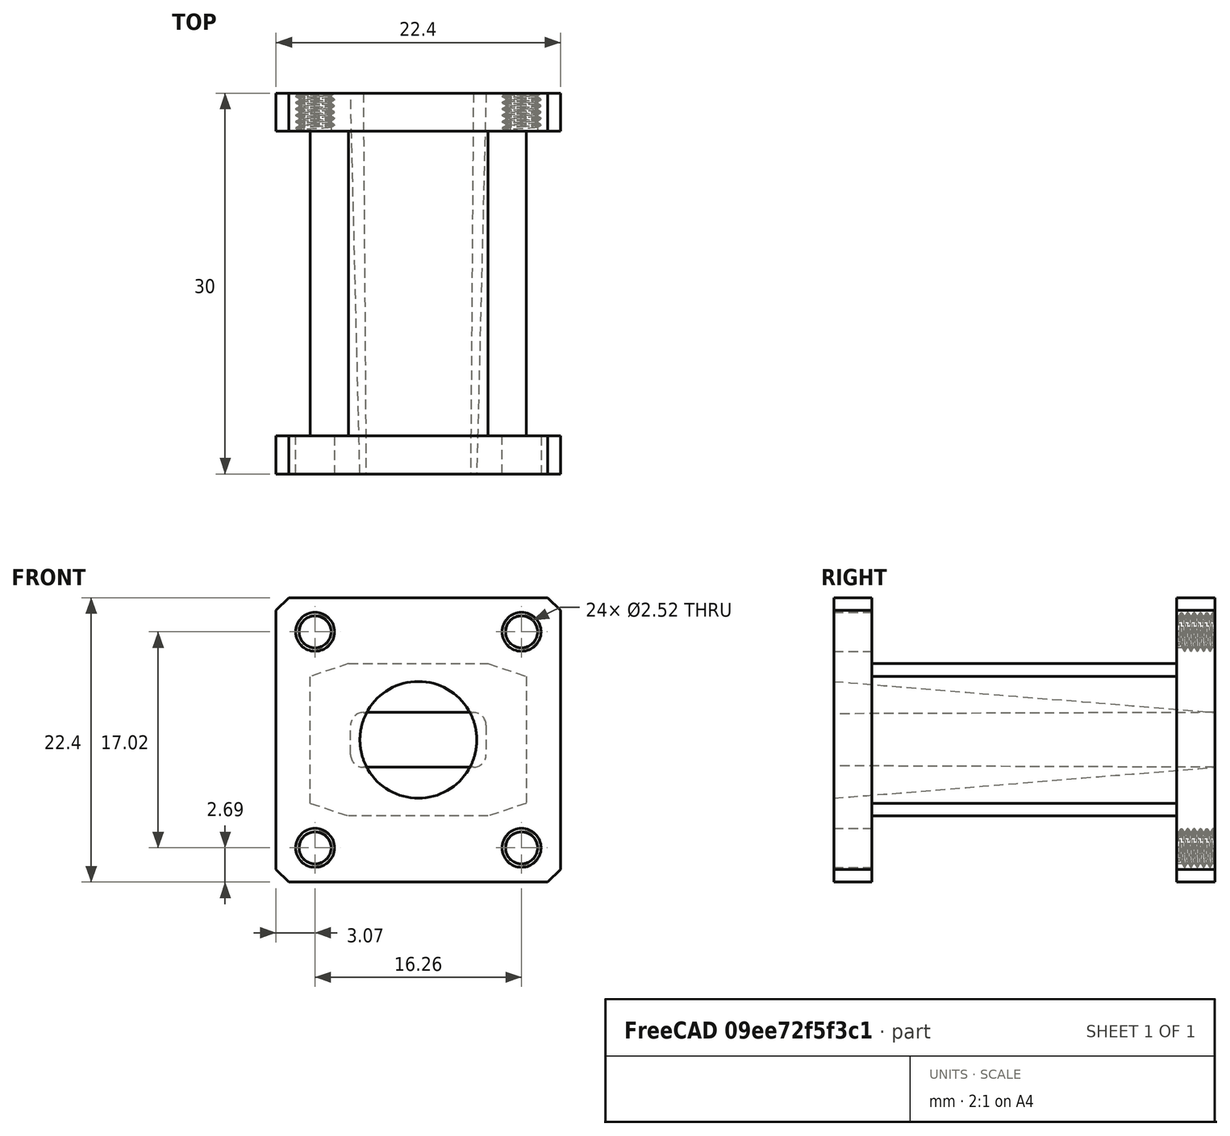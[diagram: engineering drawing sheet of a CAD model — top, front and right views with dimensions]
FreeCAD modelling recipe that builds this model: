
FCSTD DOCUMENT  (FreeCAD 0.21R33771 (Git))
Label: WR42-W1GHZ-circular
License: All rights reserved
LicenseURL: https://en.wikipedia.org/wiki/All_rights_reserved
objects: PartDesign::Chamfer×12, Sketcher::SketchObject×6, PartDesign::Pad×3, TechDraw::DrawViewBalloon×2, PartDesign::Hole×1, TechDraw::DrawSVGTemplate×1, PartDesign::SubtractiveLoft×1, PartDesign::Body×1, TechDraw::DrawViewPart×1, TechDraw::DrawPage×1
note: 41 computed .brp shape members not serialized (recipe doc carries the construction recipe); baked Part::Feature solids carry a one-line shape summary decoded from their .brp

FEATURE [Sketcher::SketchObject] Sketch
  FullyConstrained = true
  MapMode = 5
  Placement = pos=(0,0,0) rot=(1,0,0;1.5708rad)
  Support = -> [XZ_Plane]
  sketch-geometry (9):
    g0: LineSegment StartX=-11.2 StartY=11.2 StartZ=0 EndX=-11.2 EndY=-11.2 EndZ=0
    g1: LineSegment StartX=-11.2 StartY=-11.2 StartZ=0 EndX=11.2 EndY=-11.2 EndZ=0
    g2: LineSegment StartX=11.2 StartY=-11.2 StartZ=0 EndX=11.2 EndY=11.2 EndZ=0
    g3: LineSegment StartX=11.2 StartY=11.2 StartZ=0 EndX=-11.2 EndY=11.2 EndZ=0
    g4: GeomPoint X=0 Y=0 Z=0
    g5: Circle CenterX=-8.13 CenterY=8.51 CenterZ=0 NormalX=0 NormalY=0 NormalZ=1 AngleXU=0 Radius=1.535
    g6: Circle CenterX=8.13 CenterY=8.51 CenterZ=0 NormalX=0 NormalY=0 NormalZ=1 AngleXU=0 Radius=1.535
    g7: Circle CenterX=8.13 CenterY=-8.51 CenterZ=0 NormalX=0 NormalY=0 NormalZ=1 AngleXU=0 Radius=1.535
    g8: Circle CenterX=-8.13 CenterY=-8.51 CenterZ=0 NormalX=0 NormalY=0 NormalZ=1 AngleXU=0 Radius=1.535
  constraints (24):
    c: Coincident(g0,g1)
    c: Coincident(g1,g2)
    c: Coincident(g2,g3)
    c: Coincident(g3,g0)
    c: Horizontal(g1)
    c: Horizontal(g3)
    c: Vertical(g0)
    c: Vertical(g2)
    c: Symmetric(g1,g0,g4)
    c: Coincident(g4,g-1)
    c: DistanceY(g2,g2) = 22.4
    c: DistanceX(g3,g3) = 22.4
    c: Diameter(g5) = 3.07
    c: Equal(g5,g6)
    c: Equal(g5,g8)
    c: Equal(g5,g7)
    c: DistanceX(g4,g6) = 8.13
    c: DistanceX(g5,g4) = 8.13
    c: DistanceX(g8,g4) = 8.13
    c: DistanceX(g4,g7) = 8.13
    c: DistanceY(g4,g5) = 8.51
    c: DistanceY(g4,g6) = 8.51
    c: DistanceY(g7,g4) = 8.51
    c: DistanceY(g8,g4) = 8.51
FEATURE [PartDesign::Pad] Pad
  Direction = (0,-1,-2e-16)
  Length = 3
  Length2 = 10
  Placement = pos=(0,0,0) rot=(1,0,0;1.5708rad)
  Profile = -> Sketch
  ReferenceAxis = -> Sketch [N_Axis]
  Type = 0
FEATURE [PartDesign::Chamfer] Chamfer
  Angle = 45
  Base = -> Pad [Edge8]
  BaseFeature = -> Pad
  ChamferType = 0
  FlipDirection = false
  Placement = pos=(0,0,0) rot=(1,0,0;1.5708rad)
  Size = 1
  Size2 = 1
  SupportTransform = false
  UseAllEdges = false
FEATURE [PartDesign::Chamfer] Chamfer001
  Angle = 45
  Base = -> Chamfer [Edge23]
  BaseFeature = -> Chamfer
  ChamferType = 0
  FlipDirection = false
  Placement = pos=(0,0,0) rot=(1,0,0;1.5708rad)
  Size = 1
  Size2 = 1
  SupportTransform = false
  UseAllEdges = false
FEATURE [PartDesign::Chamfer] Chamfer002
  Angle = 45
  Base = -> Chamfer001 [Edge20]
  BaseFeature = -> Chamfer001
  ChamferType = 0
  FlipDirection = false
  Placement = pos=(0,0,0) rot=(1,0,0;1.5708rad)
  Size = 1
  Size2 = 1
  SupportTransform = false
  UseAllEdges = false
FEATURE [PartDesign::Chamfer] Chamfer003
  Angle = 45
  Base = -> Chamfer002 [Edge19]
  BaseFeature = -> Chamfer002
  ChamferType = 0
  FlipDirection = false
  Placement = pos=(0,0,0) rot=(1,0,0;1.5708rad)
  Size = 1
  Size2 = 1
  SupportTransform = false
  UseAllEdges = false
FEATURE [Sketcher::SketchObject] Sketch002
  FullyConstrained = true
  MapMode = 5
  Placement = pos=(0,0,0) rot=(-1,0,0;1.5708rad)
  Support = -> [Chamfer003]
  sketch-geometry (5):
    g0: LineSegment StartX=-8.5 StartY=6 StartZ=0 EndX=-8.5 EndY=-6 EndZ=0
    g1: LineSegment StartX=-8.5 StartY=-6 StartZ=0 EndX=8.5 EndY=-6 EndZ=0
    g2: LineSegment StartX=8.5 StartY=-6 StartZ=0 EndX=8.5 EndY=6 EndZ=0
    g3: LineSegment StartX=8.5 StartY=6 StartZ=0 EndX=-8.5 EndY=6 EndZ=0
    g4: GeomPoint X=0 Y=0 Z=0
  constraints (12):
    c: Coincident(g0,g1)
    c: Coincident(g1,g2)
    c: Coincident(g2,g3)
    c: Coincident(g3,g0)
    c: Horizontal(g1)
    c: Horizontal(g3)
    c: Vertical(g0)
    c: Vertical(g2)
    c: Symmetric(g1,g0,g4)
    c: Coincident(g4,g-1)
    c: DistanceX(g3,g3) = 17
    c: DistanceY(g2,g2) = 12
FEATURE [PartDesign::Pad] Pad001
  BaseFeature = -> Chamfer003
  Direction = (0,1,2e-16)
  Length = 24
  Length2 = 10
  Placement = pos=(0,0,0) rot=(1,0,0;1.5708rad)
  Profile = -> Sketch002
  ReferenceAxis = -> Sketch002 [N_Axis]
  Type = 0
FEATURE [PartDesign::Chamfer] Chamfer004
  Angle = 45
  Base = -> Pad001 [Edge42]
  BaseFeature = -> Pad001
  ChamferType = 1
  FlipDirection = false
  Placement = pos=(0,0,0) rot=(1,0,0;1.5708rad)
  Size = 3
  Size2 = 1
  SupportTransform = false
  UseAllEdges = false
FEATURE [PartDesign::Chamfer] Chamfer005
  Angle = 45
  Base = -> Chamfer004 [Edge25]
  BaseFeature = -> Chamfer004
  ChamferType = 1
  FlipDirection = false
  Placement = pos=(0,0,0) rot=(1,0,0;1.5708rad)
  Size = 1
  Size2 = 3
  SupportTransform = false
  UseAllEdges = false
FEATURE [PartDesign::Chamfer] Chamfer006
  Angle = 45
  Base = -> Chamfer005 [Edge28]
  BaseFeature = -> Chamfer005
  ChamferType = 1
  FlipDirection = false
  Placement = pos=(0,0,0) rot=(1,0,0;1.5708rad)
  Size = 3
  Size2 = 1
  SupportTransform = false
  UseAllEdges = false
FEATURE [PartDesign::Chamfer] Chamfer007
  Angle = 45
  Base = -> Chamfer006 [Edge27]
  BaseFeature = -> Chamfer006
  ChamferType = 1
  FlipDirection = false
  Placement = pos=(0,0,0) rot=(1,0,0;1.5708rad)
  Size = 1
  Size2 = 3
  SupportTransform = false
  UseAllEdges = false
FEATURE [Sketcher::SketchObject] Sketch003
  FullyConstrained = true
  MapMode = 5
  Placement = pos=(0,24,5.3e-15) rot=(-1,0,0;1.5708rad)
  Support = -> [Chamfer007]
  sketch-geometry (5):
    g0: LineSegment StartX=-11.2 StartY=11.2 StartZ=0 EndX=-11.2 EndY=-11.2 EndZ=0
    g1: LineSegment StartX=-11.2 StartY=-11.2 StartZ=0 EndX=11.2 EndY=-11.2 EndZ=0
    g2: LineSegment StartX=11.2 StartY=-11.2 StartZ=0 EndX=11.2 EndY=11.2 EndZ=0
    g3: LineSegment StartX=11.2 StartY=11.2 StartZ=0 EndX=-11.2 EndY=11.2 EndZ=0
    g4: GeomPoint X=0 Y=0 Z=0
  constraints (12):
    c: Coincident(g0,g1)
    c: Coincident(g1,g2)
    c: Coincident(g2,g3)
    c: Coincident(g3,g0)
    c: Horizontal(g1)
    c: Horizontal(g3)
    c: Vertical(g0)
    c: Vertical(g2)
    c: Symmetric(g1,g0,g4)
    c: Coincident(g4,g-1)
    c: DistanceX(g3,g3) = 22.4
    c: DistanceY(g2,g2) = 22.4
FEATURE [PartDesign::Pad] Pad002
  BaseFeature = -> Chamfer007
  Direction = (0,1,2e-16)
  Length = 3
  Length2 = 10
  Placement = pos=(0,0,0) rot=(1,0,0;1.5708rad)
  Profile = -> Sketch003
  ReferenceAxis = -> Sketch003 [N_Axis]
  Type = 0
FEATURE [PartDesign::Chamfer] Chamfer008
  Angle = 45
  Base = -> Pad002 [Edge8]
  BaseFeature = -> Pad002
  ChamferType = 0
  FlipDirection = false
  Placement = pos=(0,0,0) rot=(1,0,0;1.5708rad)
  Size = 1
  Size2 = 1
  SupportTransform = false
  UseAllEdges = false
FEATURE [PartDesign::Chamfer] Chamfer009
  Angle = 45
  Base = -> Chamfer008 [Edge3]
  BaseFeature = -> Chamfer008
  ChamferType = 0
  FlipDirection = false
  Placement = pos=(0,0,0) rot=(1,0,0;1.5708rad)
  Size = 1
  Size2 = 1
  SupportTransform = false
  UseAllEdges = false
FEATURE [PartDesign::Chamfer] Chamfer010
  Angle = 45
  Base = -> Chamfer009 [Edge26]
  BaseFeature = -> Chamfer009
  ChamferType = 0
  FlipDirection = false
  Placement = pos=(0,0,0) rot=(1,0,0;1.5708rad)
  Size = 1
  Size2 = 1
  SupportTransform = false
  UseAllEdges = false
FEATURE [PartDesign::Chamfer] Chamfer011
  Angle = 45
  Base = -> Chamfer010 [Edge23]
  BaseFeature = -> Chamfer010
  ChamferType = 0
  FlipDirection = false
  Placement = pos=(0,0,0) rot=(1,0,0;1.5708rad)
  Size = 1
  Size2 = 1
  SupportTransform = false
  UseAllEdges = false
FEATURE [Sketcher::SketchObject] Sketch004
  ExternalGeometry = -> [Chamfer011]
  FullyConstrained = true
  MapMode = 5
  Placement = pos=(0,27,8.6e-15) rot=(-1,0,0;1.5708rad)
  Support = -> [Chamfer011]
  sketch-geometry (4):
    g0: Circle CenterX=-8.13 CenterY=8.51 CenterZ=0 NormalX=0 NormalY=0 NormalZ=1 AngleXU=0 Radius=1.25
    g1: Circle CenterX=8.13 CenterY=8.51 CenterZ=0 NormalX=0 NormalY=0 NormalZ=1 AngleXU=0 Radius=1.25
    g2: Circle CenterX=8.13 CenterY=-8.51 CenterZ=0 NormalX=0 NormalY=0 NormalZ=1 AngleXU=0 Radius=1.25
    g3: Circle CenterX=-8.13 CenterY=-8.51 CenterZ=0 NormalX=0 NormalY=0 NormalZ=1 AngleXU=0 Radius=1.25
  constraints (8):
    c: Diameter(g0) = 2.5
    c: Equal(g0,g1)
    c: Equal(g0,g3)
    c: Equal(g0,g2)
    c: Coincident(g0,g-4)
    c: Coincident(g1,g-3)
    c: Coincident(g3,g-5)
    c: Coincident(g2,g-6)
FEATURE [PartDesign::Hole] Hole
  BaseFeature = -> Chamfer011
  CustomThreadClearance = 0
  Depth = 3
  DepthType = 0
  Diameter = 2.52
  DrillForDepth = false
  DrillPoint = 0
  DrillPointAngle = 118
  HoleCutCountersinkAngle = 90
  HoleCutCustomValues = false
  HoleCutDepth = 0
  HoleCutDiameter = 6.1
  HoleCutType = 0
  ModelThread = true
  Placement = pos=(0,0,0) rot=(1,0,0;1.5708rad)
  Profile = -> Sketch004
  Tapered = false
  TaperedAngle = 90
  ThreadClass = 0
  ThreadDepth = 3
  ThreadDepthType = 1
  ThreadDirection = 0
  ThreadFit = 0
  ThreadSize = 9
  ThreadType = 1
  Threaded = true
  UseCustomThreadClearance = false
FEATURE [TechDraw::DrawSVGTemplate] Template
  EditableTexts = Designed_by_Name=Dawid <owner>; Drawing_number=01; FC-Date=2024-03-14; FC-SC=n/a; FC-SH=01; FC-Title=WR42 to W1GHZ circular; Subtitle=Threads and precision perspective; Weight=n/a
  Height = 210
  Orientation = 1
  Template = <path>
  Width = 297
FEATURE [Sketcher::SketchObject] Sketch005
  FullyConstrained = true
  MapMode = 5
  Placement = pos=(0,-3,-7e-16) rot=(1,0,0;1.5708rad)
  Support = -> [Hole]
  sketch-geometry (1):
    g0: Circle CenterX=0 CenterY=0 CenterZ=0 NormalX=0 NormalY=0 NormalZ=1 AngleXU=0 Radius=4.6
  constraints (2):
    c: Coincident(g0,g-1)
    c: Diameter(g0) = 9.2
FEATURE [Sketcher::SketchObject] Sketch006
  FullyConstrained = true
  MapMode = 5
  Placement = pos=(0,27,8.6e-15) rot=(-1,0,0;1.5708rad)
  Support = -> [Hole]
  sketch-geometry (13):
    g0: LineSegment StartX=-5.334 StartY=1.159 StartZ=0 EndX=-5.334 EndY=-1.159 EndZ=0
    g1: LineSegment StartX=-4.334 StartY=-2.159 StartZ=0 EndX=4.334 EndY=-2.159 EndZ=0
    g2: LineSegment StartX=5.334 StartY=-1.159 StartZ=0 EndX=5.334 EndY=1.159 EndZ=0
    g3: LineSegment StartX=4.334 StartY=2.159 StartZ=0 EndX=-4.334 EndY=2.159 EndZ=0
    g4: GeomPoint X=0 Y=0 Z=0
    g5: ArcOfCircle CenterX=-4.334 CenterY=1.159 CenterZ=0 NormalX=0 NormalY=0 NormalZ=1 AngleXU=0 Radius=1 StartAngle=1.5708 EndAngle=3.14159
    g6: GeomPoint X=-5.334 Y=2.159 Z=0
    g7: ArcOfCircle CenterX=4.334 CenterY=1.159 CenterZ=0 NormalX=0 NormalY=0 NormalZ=1 AngleXU=0 Radius=1 StartAngle=1e-16 EndAngle=1.5708
    g8: GeomPoint X=5.334 Y=2.159 Z=0
    g9: ArcOfCircle CenterX=4.334 CenterY=-1.159 CenterZ=0 NormalX=0 NormalY=0 NormalZ=1 AngleXU=0 Radius=1 StartAngle=4.71239 EndAngle=6.28319
    g10: GeomPoint X=5.334 Y=-2.159 Z=0
    g11: ArcOfCircle CenterX=-4.334 CenterY=-1.159 CenterZ=0 NormalX=0 NormalY=0 NormalZ=1 AngleXU=0 Radius=1 StartAngle=3.14159 EndAngle=4.71239
    g12: GeomPoint X=-5.334 Y=-2.159 Z=0
  constraints (28):
    c: Horizontal(g1)
    c: Horizontal(g3)
    c: Vertical(g0)
    c: Vertical(g2)
    c: Symmetric(g10,g6,g4)
    c: Coincident(g4,g-1)
    c: PointOnObject(g6,g3)
    c: PointOnObject(g6,g0)
    c: Tangent(g3,g5) = -1.5708
    c: Tangent(g0,g5) = -1.5708
    c: PointOnObject(g8,g3)
    c: PointOnObject(g8,g2)
    c: Tangent(g3,g7) = -1.5708
    c: Tangent(g2,g7) = -1.5708
    c: PointOnObject(g10,g2)
    c: PointOnObject(g10,g1)
    c: Tangent(g2,g9) = -1.5708
    c: Tangent(g1,g9) = -1.5708
    c: PointOnObject(g12,g1)
    c: PointOnObject(g12,g0)
    c: Tangent(g1,g11) = -1.5708
    c: Tangent(g0,g11) = -1.5708
    c: Radius(g5) = 1
    c: Equal(g5,g7)
    c: Equal(g7,g9)
    c: Equal(g7,g11)
    c: DistanceY(g1,g3) = 4.318
    c: DistanceX(g0,g2) = 10.668
FEATURE [PartDesign::SubtractiveLoft] SubtractiveLoft
  BaseFeature = -> Hole
  Closed = false
  Placement = pos=(0,0,0) rot=(1,0,0;1.5708rad)
  Profile = -> Sketch006
  Ruled = false
  Sections = -> [Sketch005]
FEATURE [PartDesign::Body] Body
  Group = -> [Sketch,Pad,Chamfer,Chamfer001,Chamfer002,Chamfer003,Sketch002,Pad001,Chamfer004,Chamfer005,Chamfer006,Chamfer007,Sketch003,Pad002,Chamfer008,Chamfer009,Chamfer010,Chamfer011,Sketch004,Hole,Sketch005,Sketch006,SubtractiveLoft]
  Origin = -> Origin
  Tip = -> SubtractiveLoft
FEATURE [TechDraw::DrawViewPart] View
  CoarseView = false
  Direction = (0,1,0)
  Focus = 100
  HardHidden = false
  IsoCount = 0
  IsoHidden = false
  IsoVisible = false
  LockPosition = false
  Perspective = false
  Rotation = 0
  Scale = 4
  ScaleType = 2
  ScrubCount = 0
  SeamHidden = false
  SeamVisible = false
  SmoothHidden = false
  SmoothVisible = true
  Source = -> [SubtractiveLoft]
  X = 148.5
  XDirection = (-1,0,0)
  Y = 105
FEATURE [TechDraw::DrawViewBalloon] Balloon
  BubbleShape = 6
  EndType = 0
  EndTypeScale = 1
  KinkLength = 5
  LockPosition = false
  OriginX = -8.13
  OriginY = -8.46
  Rotation = 0
  ScaleType = 0
  ShapeScale = 1
  SourceView = -> View
  Text = 4 x M3 0,5
  TextWrapLen = -1
  X = -16.7982
  Y = -17.8186
FEATURE [TechDraw::DrawViewBalloon] Balloon001
  BubbleShape = 6
  EndType = 0
  EndTypeScale = 1
  KinkLength = 5
  LockPosition = false
  OriginX = -16.7357
  OriginY = -0.229065
  Rotation = 0
  ScaleType = 0
  ShapeScale = 1
  SourceView = -> Balloon
  Text = high precision internal dimensions
  TextWrapLen = -1
  X = 58.6236
  Y = 58.2022
FEATURE [TechDraw::DrawPage] Page  label="2D drawing"
  KeepUpdated = true
  NextBalloonIndex = 10
  ProjectionType = 0
  Template = -> Template
  Views = -> [View,Balloon,Balloon001]
note: 1 file-system path scrubbed to <path> (originals preserved in the JSON sidecar)
